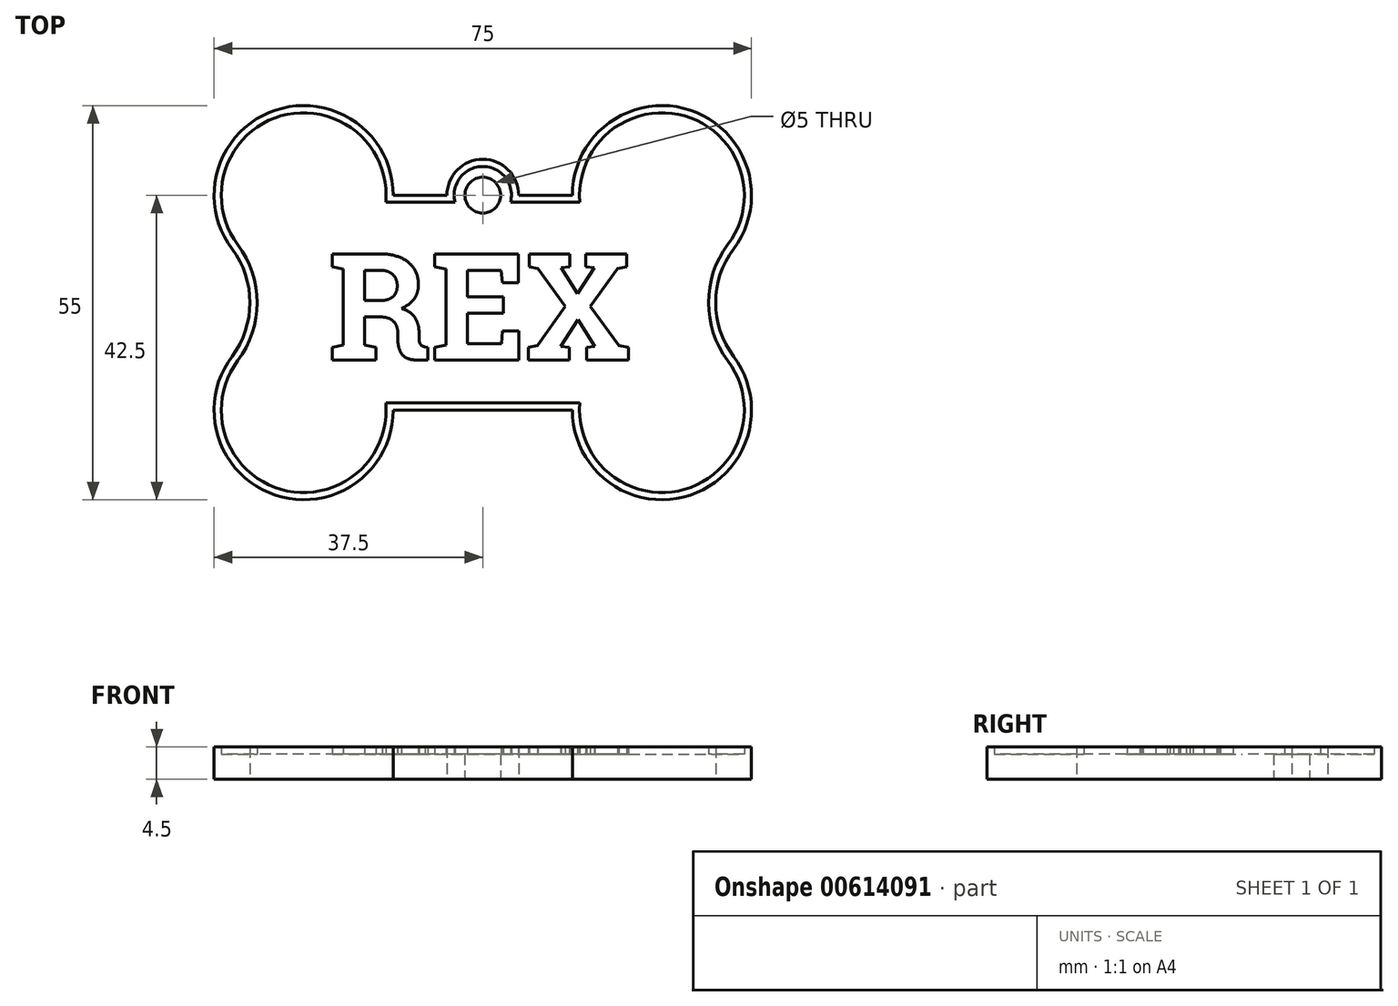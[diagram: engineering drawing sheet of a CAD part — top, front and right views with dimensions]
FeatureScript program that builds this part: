
annotation { "Feature Type Name" : "Feature", "Feature Type Description" : "" }
export const myFeature = defineFeature(function(context is Context, id is Id, definition is map)
    precondition{}
    {
        {
            var Q0;
            Q0=qCreatedBy(makeId("Top.planeOp"),FACE);
            var sketch = newSketch(context, id + "F0", { "sketchPlane" : qUnion([Q0])});
            skLineSegment(sketch, "E0", {"start": v(47.5, 30) * mm, "end": v(40, 30) * mm});
            skArc(sketch, "E1", {"start": v(22.5, 30) * mm, "mid": v(6.05, 41.86) * mm, "end": v(0, 22.5) * mm});
            skArc(sketch, "E2", {"start": v(0, 7.5) * mm, "mid": v(6.05, -11.86) * mm, "end": v(22.5, 0) * mm});
            skArc(sketch, "E3", {"start": v(47.5, 0) * mm, "mid": v(63.95, -11.86) * mm, "end": v(70, 7.5) * mm});
            skArc(sketch, "E4", {"start": v(70, 22.5) * mm, "mid": v(63.95, 41.86) * mm, "end": v(47.5, 30) * mm});
            skArc(sketch, "E5", {"start": v(0, 7.5) * mm, "mid": v(2.5, 15) * mm, "end": v(0, 22.5) * mm});
            skPoint(sketch, "E5.first.point", {"position": v(0, 22.5) * mm});
            skPoint(sketch, "E5.second.point", {"position": v(0, 7.5) * mm});
            skPoint(sketch, "E5.third.point", {"position": v(-22.5, 15) * mm});
            skPoint(sketch, "E5.third.point.positionSnap0", {"position": v(0, 15) * mm});
            skArc(sketch, "E6", {"start": v(70, 22.5) * mm, "mid": v(67.5, 15) * mm, "end": v(70, 7.5) * mm});
            skPoint(sketch, "E6.first.point", {"position": v(70, 22.5) * mm});
            skPoint(sketch, "E6.second.point", {"position": v(70, 7.5) * mm});
            skPoint(sketch, "E6.third.point", {"position": v(92.48, 14.21) * mm});
            skPoint(sketch, "E7.orphan", {"position": v(0, 30) * mm});
            skLineSegment(sketch, "E8.trimOffspring", {"start": v(22.5, 0) * mm, "end": v(47.5, 0) * mm});
            skPoint(sketch, "E9.orphan", {"position": v(0, 0) * mm});
            skLineSegment(sketch, "E10.trimOffspring", {"start": v(30, 30) * mm, "end": v(22.5, 30) * mm});
            skArc(sketch, "E11", {"start": v(40, 30) * mm, "mid": v(35, 35) * mm, "end": v(30, 30) * mm});
            skCircle(sketch, "E12", {"center": v(35, 30) * mm, "radius": 2.5 * mm});
            skSolve(sketch);
        }
        {
            var Q0;
            Q0 = qSketchRegion(id + "F0", true);
            extrude(context, id + "F1", {"entities" : qUnion([Q0]), "depth" : 3.5 * mm, "offsetDistance" : 25 * mm});
        }
        {
            var Q0;
            Q0=makeQuery(id+"F1.opExtrude","CAP_FACE",FACE,{"disambiguationData":[OSD([sQuery(id+"F0.wireOp",EDGE,"E0"),sQuery(id+"F0.wireOp",EDGE,"E1"),sQuery(id+"F0.wireOp",EDGE,"E2"),sQuery(id+"F0.wireOp",EDGE,"E3"),sQuery(id+"F0.wireOp",EDGE,"E4"),sQuery(id+"F0.wireOp",EDGE,"E5"),sQuery(id+"F0.wireOp",EDGE,"E6"),sQuery(id+"F0.wireOp",EDGE,"E8.trimOffspring"),sQuery(id+"F0.wireOp",EDGE,"E10.trimOffspring"),sQuery(id+"F0.wireOp",EDGE,"E11"),sQuery(id+"F0.wireOp",EDGE,"E12")])],"isStart":false});
            var sketch = newSketch(context, id + "F2", { "sketchPlane" : qUnion([Q0])});
            skText(sketch, "E13", { "text": "REX", "fontName": "RobotoSlab-Bold.ttf"});
            skArc(sketch, "E14.0", {"start": v(21.46, 29) * mm, "mid": v(6.84, 41.06) * mm, "end": v(0.8, 23.1) * mm});
            skLineSegment(sketch, "E14.1", {"start": v(31.13, 29) * mm, "end": v(21.46, 29) * mm});
            skArc(sketch, "E14.2", {"start": v(0.8, 23.1) * mm, "mid": v(3.5, 15) * mm, "end": v(0.8, 6.9) * mm});
            skArc(sketch, "E14.3", {"start": v(38.87, 29) * mm, "mid": v(35, 34) * mm, "end": v(31.13, 29) * mm});
            skLineSegment(sketch, "E14.4", {"start": v(48.54, 29) * mm, "end": v(38.87, 29) * mm});
            skArc(sketch, "E14.5", {"start": v(69.2, 23.1) * mm, "mid": v(63.16, 41.06) * mm, "end": v(48.54, 29) * mm});
            skArc(sketch, "E14.6", {"start": v(0.8, 6.9) * mm, "mid": v(6.84, -11.06) * mm, "end": v(21.46, 1) * mm});
            skLineSegment(sketch, "E14.7", {"start": v(21.46, 1) * mm, "end": v(48.54, 1) * mm});
            skArc(sketch, "E14.8", {"start": v(48.54, 1) * mm, "mid": v(63.16, -11.06) * mm, "end": v(69.2, 6.9) * mm});
            skArc(sketch, "E14.9", {"start": v(69.2, 6.9) * mm, "mid": v(66.5, 15) * mm, "end": v(69.2, 23.1) * mm});
            const initialGuessF2  = {"E13": [0.0134, 0.007, 1, 0, 0.015]};
            skSetInitialGuess(sketch, initialGuessF2);
            skSolve(sketch);
        }
        {
            var Q0;
            Q0=makeQuery(id+"F2.imprint","IMPRINT",FACE,{"disambiguationData":[TD([[makeQuery(id+"F2.imprint","IMPRINT",EDGE,{"derivedFrom":sQuery(id+"F2.wireOp",EDGE,"E14.0")}),-1.0]])]});
            var Q1;
            Q1=makeQuery(id+"F2.imprint","IMPRINT",FACE,{"disambiguationData":[TD([[makeQuery(id+"F2.imprint","IMPRINT",EDGE,{"derivedFrom":sQuery(id+"F2.wireOp",EDGE,"E13.sketch_text.stroke-0")}),-1.0]])]});
            var Q2;
            Q2=makeQuery(id+"F2.imprint","IMPRINT",FACE,{"disambiguationData":[TD([[makeQuery(id+"F2.imprint","IMPRINT",EDGE,{"derivedFrom":sQuery(id+"F2.wireOp",EDGE,"E13.sketch_text.stroke-36")}),-1.0]])]});
            var Q3;
            Q3=makeQuery(id+"F2.imprint","IMPRINT",FACE,{"disambiguationData":[TD([[makeQuery(id+"F2.imprint","IMPRINT",EDGE,{"derivedFrom":sQuery(id+"F2.wireOp",EDGE,"E13.sketch_text.stroke-57")}),-1.0]])]});
            extrude(context, id + "F3", {"entities" : qUnion([Q0, Q1, Q2, Q3]), "operationType" : NewBodyOperationType.ADD, "depth" : 1 * mm, "offsetDistance" : 25 * mm});
        }
    });
